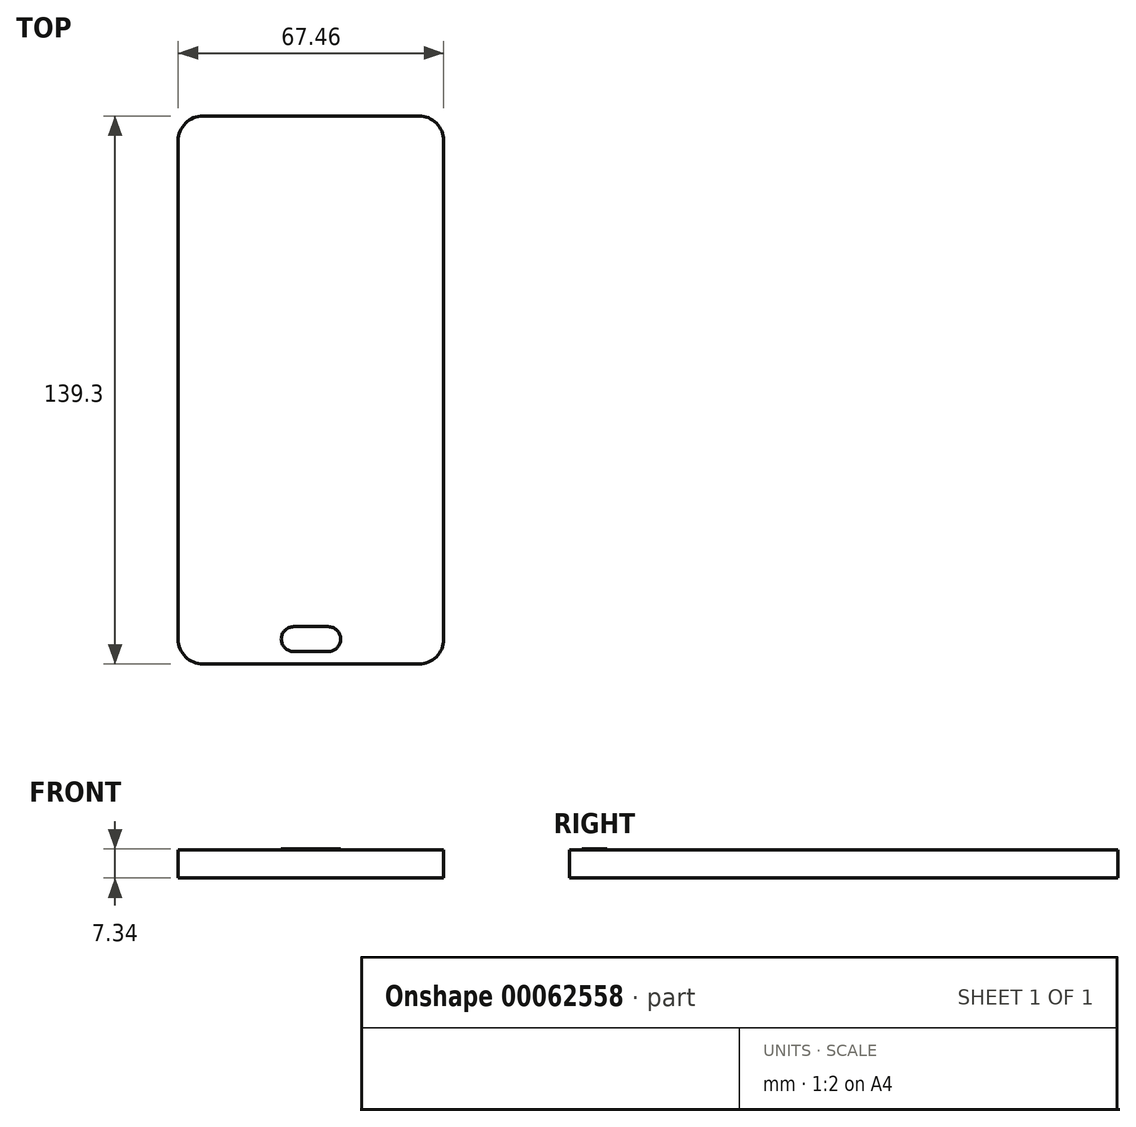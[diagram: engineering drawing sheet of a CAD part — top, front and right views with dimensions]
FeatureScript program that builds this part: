
annotation { "Feature Type Name" : "Feature", "Feature Type Description" : "" }
export const myFeature = defineFeature(function(context is Context, id is Id, definition is map)
    precondition{}
    {
        {
            var Q0;
            Q0=qCreatedBy(makeId("Top.planeOp"),FACE);
            var sketch = newSketch(context, id + "F0", { "sketchPlane" : qUnion([Q0])});
            skLineSegment(sketch, "E0.rect.bottom", {"start": v(-27.38, -69.65) * mm, "end": v(27.38, -69.65) * mm});
            skLineSegment(sketch, "E0.rect.top", {"start": v(-27.38, 69.65) * mm, "end": v(27.38, 69.65) * mm});
            skLineSegment(sketch, "E0.rect.left", {"start": v(-33.73, -63.3) * mm, "end": v(-33.73, 63.3) * mm});
            skLineSegment(sketch, "E0.rect.right", {"start": v(33.73, -63.3) * mm, "end": v(33.73, 63.3) * mm});
            skPoint(sketch, "E0.rect.middle", {"position": v(0, 0) * mm});
            skPoint(sketch, "E1.visualSharp", {"position": v(-33.73, 69.65) * mm});
            skArc(sketch, "E1.filletArc", {"start": v(-27.38, 69.65) * mm, "mid": v(-31.87, 67.8) * mm, "end": v(-33.73, 63.3) * mm});
            skPoint(sketch, "E2.visualSharp", {"position": v(33.73, 69.65) * mm});
            skArc(sketch, "E2.filletArc", {"start": v(33.73, 63.3) * mm, "mid": v(31.87, 67.8) * mm, "end": v(27.38, 69.65) * mm});
            skPoint(sketch, "E3.visualSharp", {"position": v(-33.73, -69.65) * mm});
            skArc(sketch, "E3.filletArc", {"start": v(-33.73, -63.3) * mm, "mid": v(-31.87, -67.8) * mm, "end": v(-27.38, -69.65) * mm});
            skPoint(sketch, "E4.visualSharp", {"position": v(33.73, -69.65) * mm});
            skArc(sketch, "E4.filletArc", {"start": v(27.38, -69.65) * mm, "mid": v(31.87, -67.8) * mm, "end": v(33.73, -63.3) * mm});
            skLineSegment(sketch, "E5.bottom", {"start": v(-5.55, 66.48) * mm, "end": v(5.56, 66.48) * mm});
            skLineSegment(sketch, "E5.top", {"start": v(-5.55, 64.89) * mm, "end": v(5.56, 64.89) * mm});
            skLineSegment(sketch, "E5.left", {"start": v(-6.35, 65.68) * mm, "end": v(-6.35, 65.68) * mm});
            skLineSegment(sketch, "E5.right", {"start": v(6.35, 65.68) * mm, "end": v(6.35, 65.68) * mm});
            skPoint(sketch, "E6.visualSharp", {"position": v(-6.35, 66.48) * mm});
            skArc(sketch, "E6.filletArc", {"start": v(-5.55, 66.48) * mm, "mid": v(-6.11, 66.24) * mm, "end": v(-6.35, 65.68) * mm});
            skPoint(sketch, "E7.visualSharp", {"position": v(-6.35, 64.89) * mm});
            skArc(sketch, "E7.filletArc", {"start": v(-6.35, 65.68) * mm, "mid": v(-6.11, 65.12) * mm, "end": v(-5.55, 64.89) * mm});
            skPoint(sketch, "E8.visualSharp", {"position": v(6.35, 66.48) * mm});
            skArc(sketch, "E8.filletArc", {"start": v(6.35, 65.68) * mm, "mid": v(6.12, 66.24) * mm, "end": v(5.56, 66.48) * mm});
            skPoint(sketch, "E9.visualSharp", {"position": v(6.35, 64.89) * mm});
            skArc(sketch, "E9.filletArc", {"start": v(5.56, 64.89) * mm, "mid": v(6.12, 65.12) * mm, "end": v(6.35, 65.68) * mm});
            skLineSegment(sketch, "E10.rect.bottom", {"start": v(-4.37, -60.13) * mm, "end": v(4.37, -60.13) * mm});
            skLineSegment(sketch, "E10.rect.top", {"start": v(-4.37, -66.48) * mm, "end": v(4.37, -66.48) * mm});
            skLineSegment(sketch, "E10.rect.left", {"start": v(-7.54, -63.3) * mm, "end": v(-7.54, -63.3) * mm});
            skLineSegment(sketch, "E10.rect.right", {"start": v(7.54, -63.3) * mm, "end": v(7.54, -63.3) * mm});
            skPoint(sketch, "E10.rect.middle", {"position": v(-2.43, -61.92) * mm});
            skPoint(sketch, "E11.visualSharp", {"position": v(-7.54, -60.13) * mm});
            skArc(sketch, "E11.filletArc", {"start": v(-4.37, -60.13) * mm, "mid": v(-6.61, -61.06) * mm, "end": v(-7.54, -63.3) * mm});
            skPoint(sketch, "E12.visualSharp", {"position": v(-7.54, -66.48) * mm});
            skArc(sketch, "E12.filletArc", {"start": v(-7.54, -63.3) * mm, "mid": v(-6.61, -65.55) * mm, "end": v(-4.37, -66.48) * mm});
            skPoint(sketch, "E13.visualSharp", {"position": v(7.54, -66.48) * mm});
            skArc(sketch, "E13.filletArc", {"start": v(4.37, -66.48) * mm, "mid": v(6.61, -65.55) * mm, "end": v(7.54, -63.3) * mm});
            skPoint(sketch, "E14.visualSharp", {"position": v(7.54, -60.13) * mm});
            skArc(sketch, "E14.filletArc", {"start": v(7.54, -63.3) * mm, "mid": v(6.61, -61.06) * mm, "end": v(4.37, -60.13) * mm});
            skLineSegment(sketch, "E15", {"start": v(0, -69.65) * mm, "end": v(0, -60.13) * mm, "construction": true});
            skCircle(sketch, "E16", {"center": v(-5.33, 65.69) * mm, "radius": 0.32 * mm});
            skCircle(sketch, "E17.1.0.0", {"center": v(-4.57, 65.69) * mm, "radius": 0.32 * mm});
            skCircle(sketch, "E17.2.0.0", {"center": v(-3.8, 65.69) * mm, "radius": 0.32 * mm});
            skCircle(sketch, "E17.3.0.0", {"center": v(-3.04, 65.69) * mm, "radius": 0.32 * mm});
            skCircle(sketch, "E17.4.0.0", {"center": v(-2.28, 65.69) * mm, "radius": 0.32 * mm});
            skCircle(sketch, "E17.5.0.0", {"center": v(-1.52, 65.69) * mm, "radius": 0.32 * mm});
            skCircle(sketch, "E17.6.0.0", {"center": v(-0.76, 65.69) * mm, "radius": 0.32 * mm});
            skCircle(sketch, "E17.7.0.0", {"center": v(0, 65.69) * mm, "radius": 0.32 * mm});
            skCircle(sketch, "E17.8.0.0", {"center": v(0.77, 65.69) * mm, "radius": 0.32 * mm});
            skCircle(sketch, "E17.9.0.0", {"center": v(1.53, 65.69) * mm, "radius": 0.32 * mm});
            skCircle(sketch, "E17.10.0.0", {"center": v(2.29, 65.69) * mm, "radius": 0.32 * mm});
            skCircle(sketch, "E17.11.0.0", {"center": v(3.05, 65.69) * mm, "radius": 0.32 * mm});
            skCircle(sketch, "E17.12.0.0", {"center": v(3.81, 65.69) * mm, "radius": 0.32 * mm});
            skCircle(sketch, "E17.13.0.0", {"center": v(4.58, 65.69) * mm, "radius": 0.32 * mm});
            skCircle(sketch, "E17.14.0.0", {"center": v(5.34, 65.69) * mm, "radius": 0.32 * mm});
            skLineSegment(sketch, "E17.direction1", {"start": v(-5.33, 65.69) * mm, "end": v(-4.57, 65.69) * mm, "construction": true});
            skSolve(sketch);
        }
        {
            var Q0;
            Q0=makeQuery(id+"F0.imprint","IMPRINT",FACE,{"disambiguationData":[TD([[makeQuery(id+"F0.imprint","IMPRINT",EDGE,{"derivedFrom":sQuery(id+"F0.wireOp",EDGE,"E0.rect.bottom")}),1.0]])]});
            var Q1;
            Q1=makeQuery(id+"F0.imprint","IMPRINT",FACE,{"disambiguationData":[TD([[makeQuery(id+"F0.imprint","IMPRINT",EDGE,{"derivedFrom":sQuery(id+"F0.wireOp",EDGE,"E5.bottom")}),-1.0]])]});
            extrude(context, id + "F1", {"entities" : qUnion([Q0, Q1]), "depth" : 7.14 * mm});
        }
        {
            var Q0;
            Q0=makeQuery(id+"F0.imprint","IMPRINT",FACE,{"disambiguationData":[TD([[makeQuery(id+"F0.imprint","IMPRINT",EDGE,{"derivedFrom":sQuery(id+"F0.wireOp",EDGE,"E10.rect.bottom")}),-1.0]])]});
            extrude(context, id + "F2", {"entities" : qUnion([Q0]), "operationType" : NewBodyOperationType.ADD, "depth" : 7.34 * mm});
        }
        {
            var Q0;
            Q0=makeQuery(id+"F0.imprint","IMPRINT",FACE,{"disambiguationData":[TD([[makeQuery(id+"F0.imprint","IMPRINT",EDGE,{"derivedFrom":sQuery(id+"F0.wireOp",EDGE,"E17.14.0.0")}),1.0]])]});
            var Q1;
            Q1=makeQuery(id+"F0.imprint","IMPRINT",FACE,{"disambiguationData":[TD([[makeQuery(id+"F0.imprint","IMPRINT",EDGE,{"derivedFrom":sQuery(id+"F0.wireOp",EDGE,"E17.13.0.0")}),1.0]])]});
            var Q2;
            Q2=makeQuery(id+"F0.imprint","IMPRINT",FACE,{"disambiguationData":[TD([[makeQuery(id+"F0.imprint","IMPRINT",EDGE,{"derivedFrom":sQuery(id+"F0.wireOp",EDGE,"E17.12.0.0")}),1.0]])]});
            var Q3;
            Q3=makeQuery(id+"F0.imprint","IMPRINT",FACE,{"disambiguationData":[TD([[makeQuery(id+"F0.imprint","IMPRINT",EDGE,{"derivedFrom":sQuery(id+"F0.wireOp",EDGE,"E17.11.0.0")}),1.0]])]});
            var Q4;
            Q4=makeQuery(id+"F0.imprint","IMPRINT",FACE,{"disambiguationData":[TD([[makeQuery(id+"F0.imprint","IMPRINT",EDGE,{"derivedFrom":sQuery(id+"F0.wireOp",EDGE,"E17.10.0.0")}),1.0]])]});
            var Q5;
            Q5=makeQuery(id+"F0.imprint","IMPRINT",FACE,{"disambiguationData":[TD([[makeQuery(id+"F0.imprint","IMPRINT",EDGE,{"derivedFrom":sQuery(id+"F0.wireOp",EDGE,"E17.9.0.0")}),1.0]])]});
            var Q6;
            Q6=makeQuery(id+"F0.imprint","IMPRINT",FACE,{"disambiguationData":[TD([[makeQuery(id+"F0.imprint","IMPRINT",EDGE,{"derivedFrom":sQuery(id+"F0.wireOp",EDGE,"E17.8.0.0")}),1.0]])]});
            var Q7;
            Q7=makeQuery(id+"F0.imprint","IMPRINT",FACE,{"disambiguationData":[TD([[makeQuery(id+"F0.imprint","IMPRINT",EDGE,{"derivedFrom":sQuery(id+"F0.wireOp",EDGE,"E17.7.0.0")}),1.0]])]});
            var Q8;
            Q8=makeQuery(id+"F0.imprint","IMPRINT",FACE,{"disambiguationData":[TD([[makeQuery(id+"F0.imprint","IMPRINT",EDGE,{"derivedFrom":sQuery(id+"F0.wireOp",EDGE,"E17.6.0.0")}),1.0]])]});
            var Q9;
            Q9=makeQuery(id+"F0.imprint","IMPRINT",FACE,{"disambiguationData":[TD([[makeQuery(id+"F0.imprint","IMPRINT",EDGE,{"derivedFrom":sQuery(id+"F0.wireOp",EDGE,"E17.5.0.0")}),1.0]])]});
            var Q10;
            Q10=makeQuery(id+"F0.imprint","IMPRINT",FACE,{"disambiguationData":[TD([[makeQuery(id+"F0.imprint","IMPRINT",EDGE,{"derivedFrom":sQuery(id+"F0.wireOp",EDGE,"E17.4.0.0")}),1.0]])]});
            var Q11;
            Q11=makeQuery(id+"F0.imprint","IMPRINT",FACE,{"disambiguationData":[TD([[makeQuery(id+"F0.imprint","IMPRINT",EDGE,{"derivedFrom":sQuery(id+"F0.wireOp",EDGE,"E17.3.0.0")}),1.0]])]});
            var Q12;
            Q12=makeQuery(id+"F0.imprint","IMPRINT",FACE,{"disambiguationData":[TD([[makeQuery(id+"F0.imprint","IMPRINT",EDGE,{"derivedFrom":sQuery(id+"F0.wireOp",EDGE,"E17.2.0.0")}),1.0]])]});
            var Q13;
            Q13=makeQuery(id+"F0.imprint","IMPRINT",FACE,{"disambiguationData":[TD([[makeQuery(id+"F0.imprint","IMPRINT",EDGE,{"derivedFrom":sQuery(id+"F0.wireOp",EDGE,"E17.1.0.0")}),1.0]])]});
            var Q14;
            Q14=makeQuery(id+"F0.imprint","IMPRINT",FACE,{"disambiguationData":[TD([[makeQuery(id+"F0.imprint","IMPRINT",EDGE,{"derivedFrom":sQuery(id+"F0.wireOp",EDGE,"E16")}),1.0]])]});
            extrude(context, id + "F3", {"entities" : qUnion([Q0, Q1, Q2, Q3, Q4, Q5, Q6, Q7, Q8, Q9, Q10, Q11, Q12, Q13, Q14]), "operationType" : NewBodyOperationType.ADD, "depth" : 7.14 * mm});
        }
    });
